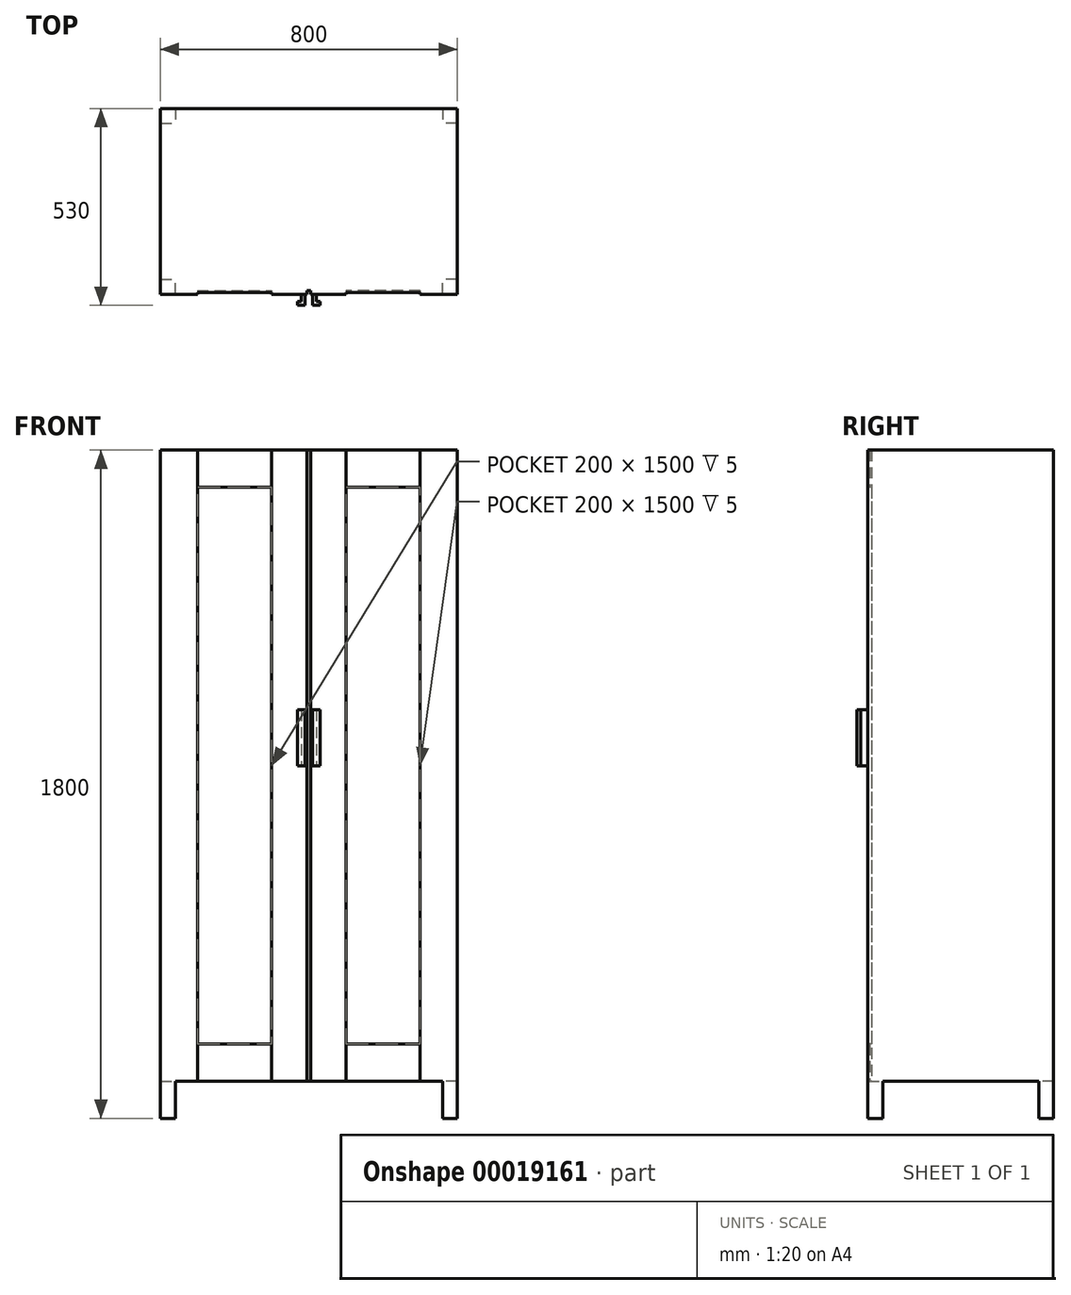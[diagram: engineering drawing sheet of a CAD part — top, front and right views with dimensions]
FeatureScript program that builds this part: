
annotation { "Feature Type Name" : "Feature", "Feature Type Description" : "" }
export const myFeature = defineFeature(function(context is Context, id is Id, definition is map)
    precondition{}
    {
        {
            var Q0;
            Q0=qCreatedBy(makeId("Top.planeOp"),FACE);
            var sketch = newSketch(context, id + "F0", { "sketchPlane" : qUnion([Q0])});
            skLineSegment(sketch, "E0.rect.bottom", {"start": v(400, 250) * mm, "end": v(-400, 250) * mm});
            skLineSegment(sketch, "E0.rect.top", {"start": v(400, -250) * mm, "end": v(-400, -250) * mm});
            skLineSegment(sketch, "E0.rect.left", {"start": v(400, 250) * mm, "end": v(400, -250) * mm});
            skLineSegment(sketch, "E0.rect.right", {"start": v(-400, 250) * mm, "end": v(-400, -250) * mm});
            skPoint(sketch, "E0.rect.middle", {"position": v(0, 0) * mm});
            skSolve(sketch);
        }
        {
            var Q0;
            Q0 = qSketchRegion(id + "F0", true);
            extrude(context, id + "F1", {"entities" : qUnion([Q0]), "depth" : 1700 * mm});
        }
        {
            var Q0;
            Q0=qCreatedBy(makeId("Top.planeOp"),FACE);
            var sketch = newSketch(context, id + "F2", { "sketchPlane" : qUnion([Q0])});
            skLineSegment(sketch, "E1.bottom", {"start": v(-400, -250) * mm, "end": v(-360, -250) * mm});
            skLineSegment(sketch, "E1.top", {"start": v(-400, -210) * mm, "end": v(-360, -210) * mm});
            skLineSegment(sketch, "E1.left", {"start": v(-400, -250) * mm, "end": v(-400, -210) * mm});
            skLineSegment(sketch, "E1.right", {"start": v(-360, -250) * mm, "end": v(-360, -210) * mm});
            skLineSegment(sketch, "E2.MirrorCS", {"start": v(400, -250) * mm, "end": v(360, -250) * mm});
            skLineSegment(sketch, "E3.MirrorCS", {"start": v(400, -210) * mm, "end": v(360, -210) * mm});
            skLineSegment(sketch, "E4.MirrorCS", {"start": v(400, -250) * mm, "end": v(400, -210) * mm});
            skLineSegment(sketch, "E5.MirrorCS", {"start": v(360, -250) * mm, "end": v(360, -210) * mm});
            skLineSegment(sketch, "E6.MirrorCS", {"start": v(400, 250) * mm, "end": v(400, 210) * mm});
            skLineSegment(sketch, "E7.MirrorCS", {"start": v(400, 210) * mm, "end": v(360, 210) * mm});
            skLineSegment(sketch, "E8.MirrorCS", {"start": v(400, 250) * mm, "end": v(360, 250) * mm});
            skLineSegment(sketch, "E9.MirrorCS", {"start": v(-360, 250) * mm, "end": v(-360, 210) * mm});
            skLineSegment(sketch, "E10.MirrorCS", {"start": v(-400, 250) * mm, "end": v(-400, 210) * mm});
            skLineSegment(sketch, "E11.MirrorCS", {"start": v(-400, 210) * mm, "end": v(-360, 210) * mm});
            skLineSegment(sketch, "E12.MirrorCS", {"start": v(-400, 250) * mm, "end": v(-360, 250) * mm});
            skLineSegment(sketch, "E13.MirrorCS", {"start": v(360, 250) * mm, "end": v(360, 210) * mm});
            skSolve(sketch);
        }
        {
            var Q0;
            Q0 = qSketchRegion(id + "F2", true);
            extrude(context, id + "F3", {"entities" : qUnion([Q0]), "operationType" : NewBodyOperationType.ADD, "oppositeDirection" : true, "depth" : 100 * mm});
        }
        {
            var Q0;
            Q0=makeQuery(id+"F1.opExtrude","SWEPT_FACE",FACE,{"disambiguationData":[OSD([sQuery(id+"F0.wireOp",EDGE,"E0.rect.top")])]});
            var sketch = newSketch(context, id + "F4", { "sketchPlane" : qUnion([Q0])});
            skLineSegment(sketch, "E14.bottom", {"start": v(-300, 1700) * mm, "end": v(-100, 1700) * mm});
            skLineSegment(sketch, "E14.top", {"start": v(-300, 0) * mm, "end": v(-100, 0) * mm});
            skLineSegment(sketch, "E14.left", {"start": v(-300, 1700) * mm, "end": v(-300, 0) * mm});
            skLineSegment(sketch, "E14.right", {"start": v(-100, 1700) * mm, "end": v(-100, 0) * mm});
            skLineSegment(sketch, "E15.MirrorCS", {"start": v(100, 1700) * mm, "end": v(100, 0) * mm});
            skLineSegment(sketch, "E16.MirrorCS", {"start": v(300, 1700) * mm, "end": v(300, 0) * mm});
            skLineSegment(sketch, "E17.MirrorCS", {"start": v(300, 0) * mm, "end": v(100, 0) * mm});
            skLineSegment(sketch, "E18.MirrorCS", {"start": v(300, 1700) * mm, "end": v(100, 1700) * mm});
            skSolve(sketch);
        }
        {
            var Q0;
            Q0 = qSketchRegion(id + "F4", true);
            extrude(context, id + "F5", {"entities" : qUnion([Q0]), "operationType" : NewBodyOperationType.REMOVE, "oppositeDirection" : true, "depth" : 5 * mm});
        }
        {
            var Q0;
            {var subQ0=sQuery(id+"F0.wireOp",EDGE,"E0.rect.top");Q0=makeQuery(id+"F5.boolean.opBoolean","SPLIT",FACE,{"disambiguationData":[TD([makeQuery(id+"F5.opExtrude","SWEPT_FACE",FACE,{"disambiguationData":[OSD([sQuery(id+"F4.wireOp",EDGE,"E14.right")])]})])],"derivedFrom":makeQuery(id+"F3.boolean.opBoolean","MERGE",FACE,{"derivedFrom":[makeQuery(id+"F1.opExtrude","SWEPT_FACE",FACE,{"disambiguationData":[OSD([subQ0])]}),makeQuery(id+"F3.opExtrude","SWEPT_FACE",FACE,{"disambiguationData":[OSD([sQuery(id+"F2.wireOp",EDGE,"E1.bottom")])]}),makeQuery(id+"F3.opExtrude","SWEPT_FACE",FACE,{"disambiguationData":[OSD([sQuery(id+"F2.wireOp",EDGE,"E2.MirrorCS")])]})]})});}
            var sketch = newSketch(context, id + "F6", { "sketchPlane" : qUnion([Q0])});
            skLineSegment(sketch, "E19.bottom", {"start": v(-300, 1600) * mm, "end": v(-100, 1600) * mm});
            skLineSegment(sketch, "E19.top", {"start": v(-300, 100) * mm, "end": v(-100, 100) * mm});
            skLineSegment(sketch, "E19.left", {"start": v(-300, 1600) * mm, "end": v(-300, 100) * mm});
            skLineSegment(sketch, "E19.right", {"start": v(-100, 1600) * mm, "end": v(-100, 100) * mm});
            skLineSegment(sketch, "E20.MirrorCS", {"start": v(300, 1600) * mm, "end": v(100, 1600) * mm});
            skLineSegment(sketch, "E21.MirrorCS", {"start": v(300, 100) * mm, "end": v(100, 100) * mm});
            skLineSegment(sketch, "E22.MirrorCS", {"start": v(100, 1600) * mm, "end": v(100, 100) * mm});
            skLineSegment(sketch, "E23.MirrorCS", {"start": v(300, 1600) * mm, "end": v(300, 100) * mm});
            skLineSegment(sketch, "E24.rect.bottom", {"start": v(5, 1700) * mm, "end": v(-5, 1700) * mm});
            skLineSegment(sketch, "E24.rect.top", {"start": v(5, 0) * mm, "end": v(-5, 0) * mm});
            skLineSegment(sketch, "E24.rect.left", {"start": v(5, 1700) * mm, "end": v(5, 0) * mm});
            skLineSegment(sketch, "E24.rect.right", {"start": v(-5, 1700) * mm, "end": v(-5, 0) * mm});
            skPoint(sketch, "E24.rect.middle", {"position": v(0, 850) * mm});
            skSolve(sketch);
        }
        {
            var Q0;
            Q0 = qSketchRegion(id + "F6", true);
            extrude(context, id + "F7", {"entities" : qUnion([Q0]), "operationType" : NewBodyOperationType.REMOVE, "oppositeDirection" : true, "depth" : 10 * mm});
        }
        {
            var Q0;
            Q0=qCreatedBy(makeId("Top.planeOp"),FACE);
            var sketch = newSketch(context, id + "F8", { "sketchPlane" : qUnion([Q0])});
            skLineSegment(sketch, "E25", {"start": v(10, -250) * mm, "end": v(10, -280) * mm});
            skLineSegment(sketch, "E26", {"start": v(10, -280) * mm, "end": v(30, -280) * mm});
            skLineSegment(sketch, "E27", {"start": v(30, -280) * mm, "end": v(30, -270) * mm});
            skLineSegment(sketch, "E28", {"start": v(30, -270) * mm, "end": v(20, -270) * mm});
            skLineSegment(sketch, "E29", {"start": v(20, -270) * mm, "end": v(20, -250) * mm});
            skLineSegment(sketch, "E30", {"start": v(20, -250) * mm, "end": v(10, -250) * mm});
            skLineSegment(sketch, "E31.MirrorCS", {"start": v(-30, -270) * mm, "end": v(-20, -270) * mm});
            skLineSegment(sketch, "E32.MirrorCS", {"start": v(-30, -280) * mm, "end": v(-30, -270) * mm});
            skLineSegment(sketch, "E33.MirrorCS", {"start": v(-20, -250) * mm, "end": v(-10, -250) * mm});
            skLineSegment(sketch, "E34.MirrorCS", {"start": v(-10, -280) * mm, "end": v(-30, -280) * mm});
            skLineSegment(sketch, "E35.MirrorCS", {"start": v(-20, -270) * mm, "end": v(-20, -250) * mm});
            skLineSegment(sketch, "E36.MirrorCS", {"start": v(-10, -250) * mm, "end": v(-10, -280) * mm});
            skSolve(sketch);
        }
        {
            var Q0;
            Q0 = qSketchRegion(id + "F8", true);
            extrude(context, id + "F9", {"entities" : qUnion([Q0]), "operationType" : NewBodyOperationType.ADD, "depth" : 1000 * mm, "hasSecondDirection" : true, "secondDirectionOppositeDirection" : false, "secondDirectionDepth" : 850 * mm});
        }
    });
